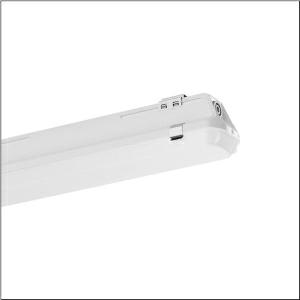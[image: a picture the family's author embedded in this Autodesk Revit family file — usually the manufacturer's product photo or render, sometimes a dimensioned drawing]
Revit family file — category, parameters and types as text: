
# Revit family: monsun_r__11_facade_51ff40mp360h_5056
name_source: partatom
category: Lighting Fixtures
units: mm (PartAtom-declared; Revit-internal decimal feet)

## family parameters
Cut with Voids When Loaded = No
Host = Face
Light Source = No
Part Type = Normal
Room Calculation Point = No
Round Connector Dimension = Use Diameter
Shared = No

## types (1)
- --- (1 x LED, 5790 lm, 33.6 W, 3000K)
    Apparent Load = 34 VA
    CIE Flux Codes = 47 77 93 95 100
    Color Rendering = 80
    Color Temperature = 3000K
    Default Elevation = 1800 mm
    Description = Monsun® 11 facade, damp-proof luminaire, chain hanger, primary optical cover: enclosure, of PMMA, light emission: direct distribution, primary light characteristic: symmetric, installation type: vertical mounting, horizontal mounting, surface-mounted, LED, rated luminous flux: 5.790lm, luminous efficacy: 172lm/W, light colour: 830, colour temperature: 3000K, control gear: ECG, with terminal, 3-pole, max. 2.5mm², mains connection: 220..240V, AC, 50/60Hz, rated input power: 34W, luminaire housing, of glass-fibre reinforced polyester, uncoated, bright grey, with climate membrane, for cables, Ø 8.4..12mm, incl. chain hanger, length: 1.590mm, width: 90mm, height: 88mm, clip for enclosure, of stainless steel (V2A), ceiling mounting element, of stainless steel (V2A), chain hanger, of stainless steel (V2A), protection rating (complete): IP66, insulation class (complete): insulation class I (protective earthing), certification: CE, ENEC, VDE, UKCA, protection symbol: D, impact resistance: IK06, permissible operating ambient temperature: -35..+50°C, standard: EN 60598-2-1, EN 50419, exposed outdoor area, contact your sales advisor before using the luminaires in applications with unclear chemical exposure, large temperature fluctuations or condensation-forming humidity, LABS conformity tested according to VDMA 24364:2018-05, packaging unit: 1 piece
    Height = 89 mm
    Lamp = 1 x LED
    Lamp Light Flux = 5790 lm
    Lamp Power = 33.6 W
    Lamp count = 1
    Length = 1590 mm
    Luminous efficacy = 172 lm/W
    Manufacturer = Siteco
    ModVariant = No
    Model = 51FF40MP360H
    Mounting Place = Ceiling
    Mounting Type = Surface mounted
    Number of Poles = 1
    OnlyDefault = Yes
    Power Factor = 1
    Product Name = Monsun® 11 facade
    Product group = damp-proof luminaire
    ProductGroupID = 301
    Protection Class = Protection class I
    Protection Degree = IP 66
    RLX_Detail_Level = 1
    RLX_Emergency_Light_Flux = 0 lm
    RLX_Emergency_Type = 0
    RLX_Emergency_Type_DB = No
    RlxData = <blob elided: 89829 chars, md5=a7ba79f2>
    Socket = socket
    Standby Power = 0 W
    System Light Flux = 5790 lm
    System Power = 34 W
    Type Comments = factory setting: luminous flux: 100 % | (A | C | E) | 77 mA
    Type Image = l_1004748.jpg
    URL = http://relux.com
    VarID = @adj_092707
    Voltage = 0 V
    Weight = 0.00 kg
    Width = 90 mm

## geometry (parser evidence)
native form markers: Blend x4, Sweep x13
no freeform markers — native parametric forms only
